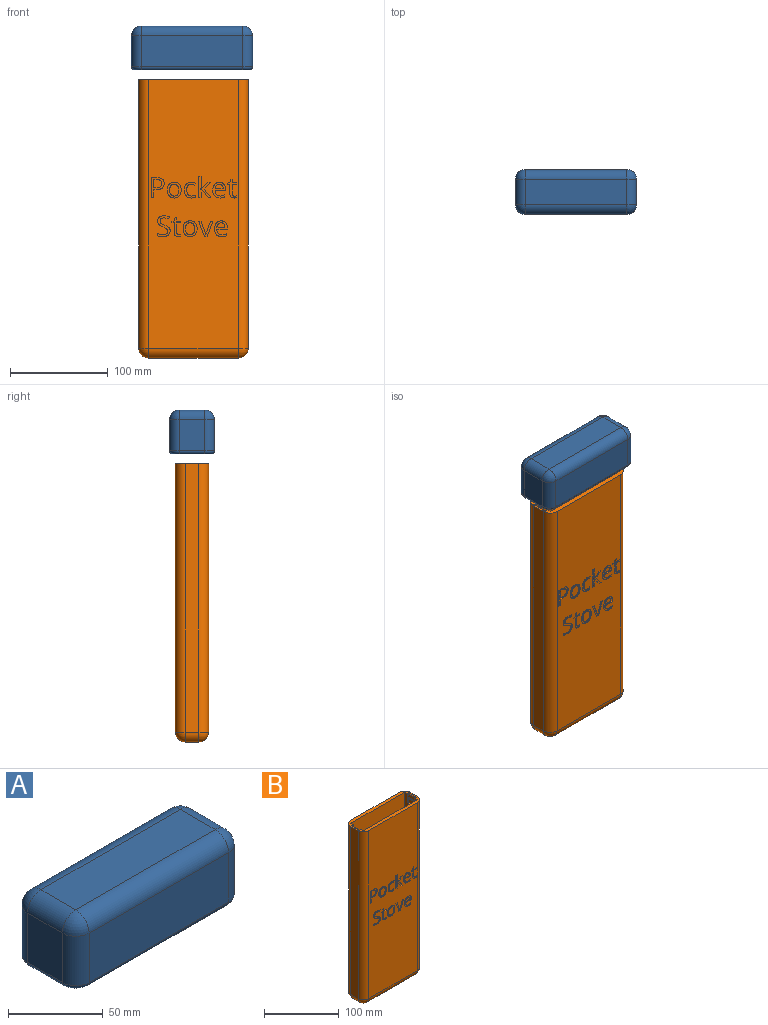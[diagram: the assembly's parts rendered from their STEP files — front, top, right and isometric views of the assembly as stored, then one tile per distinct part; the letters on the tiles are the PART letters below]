
ASSEMBLY  parts=2 mates=1
PART A: 47 faces, bbox 125.6x47.6x44.9 mm
  f0: plane 40x16mm, normal (-1,0,0), area 437.9mm2, adj f18,f19,f23,f24,f39,f41,f42,f43
  f1: plane 104x31.9mm, normal (0,1,0), area 3317.6mm2, adj f5,f8,f15,f32
  f2: plane 31.9x26mm, normal (-1,0,0), area 829.4mm2, adj f5,f6,f11,f28
  f3: plane 104x31.9mm, normal (0,-1,0), area 3317.6mm2, adj f6,f7,f12,f29
  f4: plane 31.9x26mm, normal (1,0,0), area 829.4mm2, adj f7,f8,f16,f33
  f5: cylinder r=10mm len=31.9mm, axis (0,0,-1), area 501.1mm2, adj f1,f2,f13,f30
  f6: cylinder r=10mm len=31.9mm, axis (0,0,1), area 501.1mm2, adj f2,f3,f10,f27
  f7: cylinder r=10mm len=31.9mm, axis (0,0,-1), area 501.1mm2, adj f3,f4,f14,f31
  f8: cylinder r=10mm len=31.9mm, axis (0,0,1), area 501.1mm2, adj f1,f4,f17,f34
  f9: plane 104x26mm, normal (0,0,1), area 2704mm2, adj f11,f12,f15,f16
  f10: sphere r=10mm, area 157.1mm2, adj f6,f11,f12
  f11: cylinder r=10mm len=26mm, axis (0,1,0), area 408.4mm2, adj f2,f9,f10,f13
  f12: cylinder r=10mm len=104mm, axis (-1,0,0), area 1633.6mm2, adj f3,f9,f10,f14
  f13: sphere r=10mm, area 157.1mm2, adj f5,f11,f15
  f14: sphere r=10mm, area 157.1mm2, adj f7,f12,f16
  f15: cylinder r=10mm len=104mm, axis (1,0,0), area 1633.6mm2, adj f1,f9,f13,f17
  f16: cylinder r=10mm len=26mm, axis (0,-1,0), area 408.4mm2, adj f4,f9,f14,f17
  f17: sphere r=10mm, area 157.1mm2, adj f8,f15,f16
  f18: plane 118x40mm, normal (0,0,-1), area 659.8mm2, adj f0,f20,f21,f22,f23,f24,f25,f26
  f19: plane 114x36mm, normal (0,0,-1), area 3883.2mm2, adj f0,f20,f21,f22,f23,f24,f25,f26
  f20: plane 40x16mm, normal (1,0,0), area 437.9mm2, adj f18,f19,f21,f26,f36,f37,f38,f45
  f21: cylinder r=10mm len=40mm, axis (0,0,-1), area 628.3mm2, adj f18,f19,f20,f22
  f22: plane 94x40mm, normal (0,-1,0), area 3760mm2, adj f18,f19,f21,f23
  f23: cylinder r=10mm len=40mm, axis (0,0,-1), area 628.3mm2, adj f0,f18,f19,f22
  f24: cylinder r=10mm len=40mm, axis (0,0,-1), area 628.3mm2, adj f0,f18,f19,f25
  f25: plane 94x40mm, normal (0,1,0), area 3760mm2, adj f18,f19,f24,f26
  f26: cylinder r=10mm len=40mm, axis (0,0,-1), area 628.3mm2, adj f18,f19,f20,f25
  f27: torus R=7mm, axis (0,0,1), area 66mm2, adj f6,f18,f28,f29
  f28: cylinder r=3mm len=26mm, axis (0,-1,0), area 122.5mm2, adj f2,f18,f27,f30
  f29: cylinder r=3mm len=104mm, axis (1,0,0), area 490.1mm2, adj f3,f18,f27,f31
  f30: torus R=7mm, axis (0,0,1), area 66mm2, adj f5,f18,f28,f32
  f31: torus R=7mm, axis (0,0,1), area 66mm2, adj f7,f18,f29,f33
  f32: cylinder r=3mm len=104mm, axis (-1,0,0), area 490.1mm2, adj f1,f18,f30,f34
  f33: cylinder r=3mm len=26mm, axis (0,1,0), area 122.5mm2, adj f4,f18,f31,f34
  f34: torus R=7mm, axis (0,0,1), area 66mm2, adj f8,f18,f32,f33
  f35: plane 15x13.5mm, normal (1,0,0), area 202.1mm2, adj f19,f36,f37,f38,f45,f46
  f36: plane 14x5mm, normal (0,-1,0), area 70mm2, adj f19,f20,f35,f45
  f37: plane 14x5mm, normal (0,1,0), area 70mm2, adj f19,f20,f35,f46
  f38: plane 11.5x5mm, normal (0,0,-1), area 57.5mm2, adj f20,f35,f45,f46
  f39: plane 14x5mm, normal (0,-1,0), area 70mm2, adj f0,f19,f40,f44
  f40: plane 15x13.5mm, normal (-1,0,0), area 202.1mm2, adj f19,f39,f41,f42,f43,f44
  f41: plane 14x5mm, normal (0,1,0), area 70mm2, adj f0,f19,f40,f43
  f42: plane 11.5x5mm, normal (0,0,-1), area 57.5mm2, adj f0,f40,f43,f44
  f43: cylinder r=1mm len=5mm, axis (-1,0,0), area 7.9mm2, adj f0,f40,f41,f42
  f44: cylinder r=1mm len=5mm, axis (1,0,0), area 7.9mm2, adj f0,f39,f40,f42
  f45: cylinder r=1mm len=5mm, axis (1,0,0), area 7.9mm2, adj f20,f35,f36,f38
  f46: cylinder r=1mm len=5mm, axis (-1,0,0), area 7.9mm2, adj f20,f35,f37,f38
PART B: 255 faces, bbox 112x34x285 mm
  f0: plane 14x6.27mm, normal (-1,0,0), area 77.1mm2, adj f5,f6,f32,f241,f242,f253
  f1: plane 14x5.12mm, normal (-1,0,0), area 71.6mm2, adj f5,f6,f245,f252
  f2: plane 14x6.27mm, normal (1,0,0), area 77.1mm2, adj f4,f30,f31,f239,f240,f254
  f3: plane 14x5.12mm, normal (1,0,0), area 71.6mm2, adj f30,f31,f246,f249
  f4: plane 4x2mm, normal (0,0,1), area 8mm2, adj f2,f10,f239,f240
  f5: plane 8.8x2.55mm, normal (0,-1,0), area 18.2mm2, adj f0,f1,f12,f241,f244,f245,f250,f253
  f6: plane 8.8x2.55mm, normal (0,1,0), area 18.2mm2, adj f0,f1,f12,f242,f244,f245,f251,f253
  f7: plane 275x92mm, normal (0,-1,0), area 24044.4mm2, adj f16,f18,f20,f21,f33,f34,f35,f36
  f8: plane 275x14mm, normal (-1,0,0), area 3850mm2, adj f16,f20,f26,f29
  f9: plane 275x14mm, normal (1,0,0), area 3850mm2, adj f16,f18,f22,f23
  f10: plane 280x24mm, normal (1,0,0), area 6520.1mm2, adj f4,f13,f14,f16,f17,f30,f31,f239
  f11: plane 92x14mm, normal (0,0,-1), area 1288mm2, adj f21,f22,f26,f27
  f12: plane 280x24mm, normal (-1,0,0), area 6520.1mm2, adj f5,f6,f13,f14,f16,f17,f32,f241
  f13: plane 280x102mm, normal (0,-1,0), area 28560mm2, adj f10,f12,f16,f17
  f14: plane 280x102mm, normal (0,1,0), area 28560mm2, adj f10,f12,f16,f17
  f15: plane 275x92mm, normal (0,1,0), area 25300mm2, adj f16,f23,f27,f29
  f16: plane 112x34mm, normal (0,0,1), area 1169.2mm2, adj f7,f8,f9,f10,f12,f13,f14,f15
  f17: plane 102x24mm, normal (0,0,1), area 2448mm2, adj f10,f12,f13,f14
  f18: cylinder r=10mm len=275mm, axis (0,0,-1), area 4319.7mm2, adj f7,f9,f16,f19
  f19: sphere r=10mm, area 157.1mm2, adj f18,f21,f22
  f20: cylinder r=10mm len=275mm, axis (0,0,1), area 4319.7mm2, adj f7,f8,f16,f24
  f21: cylinder r=10mm len=92mm, axis (1,0,0), area 1445.1mm2, adj f7,f11,f19,f24
  f22: cylinder r=10mm len=14mm, axis (0,1,0), area 219.9mm2, adj f9,f11,f19,f25
  f23: cylinder r=10mm len=275mm, axis (0,0,1), area 4319.7mm2, adj f9,f15,f16,f25
  f24: sphere r=10mm, area 157.1mm2, adj f20,f21,f26
  f25: sphere r=10mm, area 157.1mm2, adj f22,f23,f27
  f26: cylinder r=10mm len=14mm, axis (0,-1,0), area 219.9mm2, adj f8,f11,f24,f28
  f27: cylinder r=10mm len=92mm, axis (-1,0,0), area 1445.1mm2, adj f11,f15,f25,f28
  f28: sphere r=10mm, area 157.1mm2, adj f26,f27,f29
  f29: cylinder r=10mm len=275mm, axis (0,0,-1), area 4319.7mm2, adj f8,f15,f16,f28
  f30: plane 8.8x2.55mm, normal (0,-1,0), area 18.2mm2, adj f2,f3,f10,f239,f243,f246,f247,f254
  f31: plane 8.8x2.55mm, normal (0,1,0), area 18.2mm2, adj f2,f3,f10,f240,f243,f246,f248,f254
  f32: plane 4x2mm, normal (0,0,1), area 8mm2, adj f0,f12,f241,f242
  f33: extruded ~5.23x2.08mm, area 5.8mm2, adj f7,f34,f47,f48
  f34: extruded ~3.93x1mm, area 4.1mm2, adj f7,f33,f35,f48
  f35: plane 2.08x1mm, normal (-1,0,0), area 2.1mm2, adj f7,f34,f36,f48
  f36: extruded ~3.99x1mm, area 4.1mm2, adj f7,f35,f37,f48
  f37: extruded ~3.43x1.53mm, area 3.9mm2, adj f7,f36,f38,f48
  f38: extruded ~4.4x1.16mm, area 4.6mm2, adj f7,f37,f39,f48
  f39: extruded ~6.05x4.74mm, area 8.8mm2, adj f7,f38,f40,f48
  f40: extruded ~1.63x1mm, area 1.6mm2, adj f7,f39,f41,f48
  f41: extruded ~1.7x1mm, area 1.8mm2, adj f7,f40,f42,f48
  f42: plane 2x1mm, normal (-0.94,0,0.34), area 2.1mm2, adj f7,f41,f43,f48
  f43: extruded ~1.76x1mm, area 1.9mm2, adj f7,f42,f44,f48
  f44: extruded ~2.24x1mm, area 2.3mm2, adj f7,f43,f45,f48
  f45: extruded ~5.36x2.13mm, area 6mm2, adj f7,f44,f46,f48
  f46: extruded ~6.03x1.88mm, area 6.5mm2, adj f7,f45,f47,f48
  f47: extruded ~5.89x1.85mm, area 6.3mm2, adj f7,f33,f46,f48
  f48: plane 16.13x11.24mm, normal (0,-1,0), area 64.2mm2, adj f33,f34,f35,f36,f37,f38,f39,f40
  f49: extruded ~2.99x1.22mm, area 3.3mm2, adj f50,f67,f68,f234
  f50: extruded ~2.84x1.19mm, area 3.2mm2, adj f49,f51,f68,f234
  f51: extruded ~3.41x1mm, area 3.6mm2, adj f50,f52,f68,f234
  f52: plane 8.13x1mm, normal (0,0,-1), area 8.1mm2, adj f51,f67,f68,f234
  f53: extruded ~5.44x2.1mm, area 6mm2, adj f7,f54,f66,f68
  f54: extruded ~2.69x1mm, area 2.7mm2, adj f7,f53,f55,f68
  f55: extruded ~2.36x1mm, area 2.5mm2, adj f7,f54,f56,f68
  f56: plane 2.1x1mm, normal (-1,0,0), area 2.1mm2, adj f7,f55,f57,f68
  f57: extruded ~4.96x1.05mm, area 5.1mm2, adj f7,f56,f58,f68
  f58: extruded ~3.7x1.42mm, area 4.1mm2, adj f7,f57,f59,f68
  f59: extruded ~4.16x1.39mm, area 4.5mm2, adj f7,f58,f60,f68
  f60: plane 10.71x1mm, normal (0,0,1), area 10.7mm2, adj f7,f59,f61,f68
  f61: plane 1.49x1mm, normal (-1,0,0), area 1.5mm2, adj f7,f60,f62,f68
  f62: extruded ~5.08x1.7mm, area 5.5mm2, adj f7,f61,f63,f68
  f63: extruded ~4.62x1.92mm, area 5.2mm2, adj f7,f62,f64,f68
  f64: extruded ~4.98x2.21mm, area 5.6mm2, adj f7,f63,f65,f68
  f65: extruded ~5.98x1.85mm, area 6.4mm2, adj f7,f64,f66,f68
  f66: extruded ~5.83x2mm, area 6.3mm2, adj f7,f53,f65,f68
  f67: extruded ~3.38x1.32mm, area 3.7mm2, adj f49,f52,f68,f234
  f68: plane 16.13x13.16mm, normal (0,-1,0), area 96.5mm2, adj f49,f50,f51,f52,f53,f54,f55,f56
  f69: extruded ~4.54x1.19mm, area 4.8mm2, adj f70,f85,f86,f235
  f70: extruded ~4.53x1.18mm, area 4.8mm2, adj f69,f71,f86,f235
  f71: extruded ~3.49x1.52mm, area 4mm2, adj f70,f72,f86,f235
  f72: extruded ~3.54x1.54mm, area 4mm2, adj f71,f73,f86,f235
  f73: extruded ~4.51x1.2mm, area 4.7mm2, adj f72,f74,f86,f235
  f74: extruded ~4.55x1.2mm, area 4.8mm2, adj f73,f75,f86,f235
  f75: extruded ~3.52x1.55mm, area 4mm2, adj f74,f85,f86,f235
  f76: extruded ~5.94x1.91mm, area 6.4mm2, adj f7,f77,f84,f86
  f77: extruded ~5.88x1.92mm, area 6.3mm2, adj f7,f76,f78,f86
  f78: extruded ~5.18x2.17mm, area 5.8mm2, adj f7,f77,f79,f86
  f79: extruded ~5.28x2.12mm, area 5.9mm2, adj f7,f78,f80,f86
  f80: extruded ~5.93x1.9mm, area 6.4mm2, adj f7,f79,f81,f86
  f81: extruded ~4.29x1mm, area 4.4mm2, adj f7,f80,f82,f86
  f82: extruded ~2.81x2.5mm, area 3.8mm2, adj f7,f81,f83,f86
  f83: extruded ~3.71x1mm, area 3.9mm2, adj f7,f82,f84,f86
  f84: extruded ~5.29x2.14mm, area 5.9mm2, adj f7,f76,f83,f86
  f85: extruded ~3.5x1.56mm, area 4mm2, adj f69,f75,f86,f235
  f86: plane 16.13x14.29mm, normal (0,-1,0), area 93mm2, adj f69,f70,f71,f72,f73,f74,f75,f76
  f87: extruded ~2.27x1.86mm, area 2.9mm2, adj f7,f88,f101,f102
  f88: plane 1x0.11mm, normal (0,0,-1), area 0.1mm2, adj f7,f87,f89,f102
  f89: extruded ~2.41x1mm, area 2.4mm2, adj f7,f88,f90,f102
  f90: plane 11.71x1mm, normal (-1,0,0), area 11.7mm2, adj f7,f89,f91,f102
  f91: plane 2.33x1mm, normal (0,0,-1), area 2.3mm2, adj f7,f90,f92,f102
  f92: plane 22.09x1mm, normal (1,0,0), area 22.1mm2, adj f7,f91,f93,f102
  f93: plane 2.33x1mm, normal (0,0,1), area 2.3mm2, adj f7,f92,f94,f102
  f94: plane 5.82x1mm, normal (-1,0,0), area 5.8mm2, adj f7,f93,f95,f102
  f95: plane 1.77x1.54mm, normal (-0.65,0,0.76), area 2.3mm2, adj f7,f94,f96,f102
  f96: plane 7.35x5.5mm, normal (0.8,0,0.6), area 9.2mm2, adj f7,f95,f97,f102
  f97: plane 2.85x1mm, normal (0,0,1), area 2.9mm2, adj f7,f96,f98,f102
  f98: plane 8.93x6.74mm, normal (-0.8,0,-0.6), area 11.2mm2, adj f7,f97,f99,f102
  f99: plane 6.63x6.3mm, normal (-0.72,0,0.69), area 9.1mm2, adj f7,f98,f100,f102
  f100: plane 2.8x1mm, normal (0,0,-1), area 2.8mm2, adj f7,f99,f101,f102
  f101: plane 5.32x5.02mm, normal (0.73,0,-0.69), area 7.3mm2, adj f7,f87,f100,f102
  f102: plane 22.09x12.45mm, normal (0,-1,0), area 97.7mm2, adj f87,f88,f89,f90,f91,f92,f93,f94
  f103: extruded ~1.21x1mm, area 1.2mm2, adj f7,f104,f121,f122
  f104: extruded ~1.83x1mm, area 2mm2, adj f7,f103,f105,f122
  f105: extruded ~2.16x1mm, area 2.3mm2, adj f7,f104,f106,f122
  f106: plane 9.16x1mm, normal (-1,0,0), area 9.2mm2, adj f7,f105,f107,f122
  f107: plane 4.51x1mm, normal (0,0,1), area 4.5mm2, adj f7,f106,f108,f122
  f108: plane 1.83x1mm, normal (-1,0,0), area 1.8mm2, adj f7,f107,f109,f122
  f109: plane 4.51x1mm, normal (0,0,-1), area 4.5mm2, adj f7,f108,f110,f122
  f110: plane 3.61x1mm, normal (-1,0,0), area 3.6mm2, adj f7,f109,f111,f122
  f111: plane 1.36x1mm, normal (0,0,-1), area 1.4mm2, adj f7,f110,f112,f122
  f112: plane 3.32x1mm, normal (0.96,0,-0.29), area 3.5mm2, adj f7,f111,f113,f122
  f113: plane 2.23x1mm, normal (0.4,0,-0.92), area 2.4mm2, adj f7,f112,f114,f122
  f114: plane 1.14x1mm, normal (1,0,0), area 1.1mm2, adj f7,f113,f115,f122
  f115: plane 2.23x1mm, normal (0,0,1), area 2.2mm2, adj f7,f114,f116,f122
  f116: plane 9.26x1mm, normal (1,0,0), area 9.3mm2, adj f7,f115,f117,f122
  f117: extruded ~4.76x4.51mm, area 7.5mm2, adj f7,f116,f118,f122
  f118: extruded ~1.34x1mm, area 1.4mm2, adj f7,f117,f119,f122
  f119: extruded ~1.13x1mm, area 1.2mm2, adj f7,f118,f120,f122
  f120: plane 1.8x1mm, normal (-1,0,0), area 1.8mm2, adj f7,f119,f121,f122
  f121: extruded ~1x0.92mm, area 0.9mm2, adj f7,f103,f120,f122
  f122: plane 19.45x9.21mm, normal (0,-1,0), area 62.6mm2, adj f103,f104,f105,f106,f107,f108,f109,f110
  f123: extruded ~4.27x1.99mm, area 4.9mm2, adj f7,f124,f147,f148
  f124: extruded ~3.46x1.23mm, area 3.8mm2, adj f7,f123,f125,f148
  f125: extruded ~4.49x2.5mm, area 5.2mm2, adj f7,f124,f126,f148
  f126: extruded ~2.89x1.27mm, area 3.2mm2, adj f7,f125,f127,f148
  f127: extruded ~1.34x1.27mm, area 1.9mm2, adj f7,f126,f128,f148
  f128: extruded ~1.77x1mm, area 1.8mm2, adj f7,f127,f129,f148
  f129: extruded ~2.28x1.08mm, area 2.6mm2, adj f7,f128,f130,f148
  f130: extruded ~3x1mm, area 3.2mm2, adj f7,f129,f131,f148
  f131: extruded ~5x1.08mm, area 5.1mm2, adj f7,f130,f132,f148
  f132: plane 2.1x1mm, normal (-0.94,0,0.34), area 2.2mm2, adj f7,f131,f133,f148
  f133: extruded ~5.69x1.14mm, area 5.8mm2, adj f7,f132,f134,f148
  f134: extruded ~4.77x1.42mm, area 5.1mm2, adj f7,f133,f135,f148
  f135: extruded ~3.82x1.8mm, area 4.4mm2, adj f7,f134,f136,f148
  f136: extruded ~3.7x1.24mm, area 4mm2, adj f7,f135,f137,f148
  f137: extruded ~4.14x2.46mm, area 4.9mm2, adj f7,f136,f138,f148
  f138: extruded ~3.09x1.32mm, area 3.4mm2, adj f7,f137,f139,f148
  f139: extruded ~1.45x1.27mm, area 1.9mm2, adj f7,f138,f140,f148
  f140: extruded ~1.76x1mm, area 1.8mm2, adj f7,f139,f141,f148
  f141: extruded ~2.55x1.22mm, area 2.9mm2, adj f7,f140,f142,f148
  f142: extruded ~3.63x1mm, area 3.8mm2, adj f7,f141,f143,f148
  f143: extruded ~2.98x1mm, area 3mm2, adj f7,f142,f144,f148
  f144: extruded ~2.78x1mm, area 2.9mm2, adj f7,f143,f145,f148
  f145: plane 2.33x1mm, normal (1,0,0), area 2.3mm2, adj f7,f144,f146,f148
  f146: extruded ~5.68x1mm, area 5.8mm2, adj f7,f145,f147,f148
  f147: extruded ~5.39x1.54mm, area 5.7mm2, adj f7,f123,f146,f148
  f148: plane 21.33x13.06mm, normal (0,-1,0), area 99.7mm2, adj f123,f124,f125,f126,f127,f128,f129,f130
  f149: extruded ~1.21x1mm, area 1.2mm2, adj f7,f150,f167,f168
  f150: extruded ~1.83x1mm, area 2mm2, adj f7,f149,f151,f168
  f151: extruded ~2.16x1mm, area 2.3mm2, adj f7,f150,f152,f168
  f152: plane 9.16x1mm, normal (-1,0,0), area 9.2mm2, adj f7,f151,f153,f168
  f153: plane 4.51x1mm, normal (0,0,1), area 4.5mm2, adj f7,f152,f154,f168
  f154: plane 1.83x1mm, normal (-1,0,0), area 1.8mm2, adj f7,f153,f155,f168
  f155: plane 4.51x1mm, normal (0,0,-1), area 4.5mm2, adj f7,f154,f156,f168
  f156: plane 3.61x1mm, normal (-1,0,0), area 3.6mm2, adj f7,f155,f157,f168
  f157: plane 1.36x1mm, normal (0,0,-1), area 1.4mm2, adj f7,f156,f158,f168
  f158: plane 3.32x1mm, normal (0.96,0,-0.29), area 3.5mm2, adj f7,f157,f159,f168
  f159: plane 2.23x1mm, normal (0.4,0,-0.92), area 2.4mm2, adj f7,f158,f160,f168
  f160: plane 1.14x1mm, normal (1,0,0), area 1.1mm2, adj f7,f159,f161,f168
  f161: plane 2.23x1mm, normal (0,0,1), area 2.2mm2, adj f7,f160,f162,f168
  f162: plane 9.26x1mm, normal (1,0,0), area 9.3mm2, adj f7,f161,f163,f168
  f163: extruded ~4.76x4.51mm, area 7.5mm2, adj f7,f162,f164,f168
  f164: extruded ~1.34x1mm, area 1.4mm2, adj f7,f163,f165,f168
  f165: extruded ~1.13x1mm, area 1.2mm2, adj f7,f164,f166,f168
  f166: plane 1.8x1mm, normal (-1,0,0), area 1.8mm2, adj f7,f165,f167,f168
  f167: extruded ~1x0.92mm, area 0.9mm2, adj f7,f149,f166,f168
  f168: plane 19.45x9.21mm, normal (0,-1,0), area 62.6mm2, adj f149,f150,f151,f152,f153,f154,f155,f156
  f169: extruded ~2.99x1.22mm, area 3.3mm2, adj f170,f187,f188,f236
  f170: extruded ~2.84x1.19mm, area 3.2mm2, adj f169,f171,f188,f236
  f171: extruded ~3.41x1mm, area 3.6mm2, adj f170,f172,f188,f236
  f172: plane 8.13x1mm, normal (0,0,-1), area 8.1mm2, adj f171,f187,f188,f236
  f173: extruded ~5.44x2.1mm, area 6mm2, adj f7,f174,f186,f188
  f174: extruded ~2.69x1mm, area 2.7mm2, adj f7,f173,f175,f188
  f175: extruded ~2.36x1mm, area 2.5mm2, adj f7,f174,f176,f188
  f176: plane 2.1x1mm, normal (-1,0,0), area 2.1mm2, adj f7,f175,f177,f188
  f177: extruded ~4.96x1.05mm, area 5.1mm2, adj f7,f176,f178,f188
  f178: extruded ~3.7x1.42mm, area 4.1mm2, adj f7,f177,f179,f188
  f179: extruded ~4.16x1.39mm, area 4.5mm2, adj f7,f178,f180,f188
  f180: plane 10.71x1mm, normal (0,0,1), area 10.7mm2, adj f7,f179,f181,f188
  f181: plane 1.49x1mm, normal (-1,0,0), area 1.5mm2, adj f7,f180,f182,f188
  f182: extruded ~5.08x1.7mm, area 5.5mm2, adj f7,f181,f183,f188
  f183: extruded ~4.62x1.92mm, area 5.2mm2, adj f7,f182,f184,f188
  f184: extruded ~4.98x2.21mm, area 5.6mm2, adj f7,f183,f185,f188
  f185: extruded ~5.98x1.85mm, area 6.4mm2, adj f7,f184,f186,f188
  f186: extruded ~5.83x2mm, area 6.3mm2, adj f7,f173,f185,f188
  f187: extruded ~3.38x1.32mm, area 3.7mm2, adj f169,f172,f188,f236
  f188: plane 16.13x13.16mm, normal (0,-1,0), area 96.5mm2, adj f169,f170,f171,f172,f173,f174,f175,f176
  f189: extruded ~4.54x1.19mm, area 4.8mm2, adj f190,f205,f206,f237
  f190: extruded ~4.53x1.18mm, area 4.8mm2, adj f189,f191,f206,f237
  f191: extruded ~3.49x1.52mm, area 4mm2, adj f190,f192,f206,f237
  f192: extruded ~3.54x1.54mm, area 4mm2, adj f191,f193,f206,f237
  f193: extruded ~4.51x1.2mm, area 4.7mm2, adj f192,f194,f206,f237
  f194: extruded ~4.55x1.2mm, area 4.8mm2, adj f193,f195,f206,f237
  f195: extruded ~3.52x1.55mm, area 4mm2, adj f194,f205,f206,f237
  f196: extruded ~5.94x1.91mm, area 6.4mm2, adj f7,f197,f204,f206
  f197: extruded ~5.88x1.92mm, area 6.3mm2, adj f7,f196,f198,f206
  f198: extruded ~5.18x2.17mm, area 5.8mm2, adj f7,f197,f199,f206
  f199: extruded ~5.28x2.12mm, area 5.9mm2, adj f7,f198,f200,f206
  f200: extruded ~5.93x1.9mm, area 6.4mm2, adj f7,f199,f201,f206
  f201: extruded ~4.29x1mm, area 4.4mm2, adj f7,f200,f202,f206
  f202: extruded ~2.81x2.5mm, area 3.8mm2, adj f7,f201,f203,f206
  f203: extruded ~3.71x1mm, area 3.9mm2, adj f7,f202,f204,f206
  f204: extruded ~5.29x2.14mm, area 5.9mm2, adj f7,f196,f203,f206
  f205: extruded ~3.5x1.56mm, area 4mm2, adj f189,f195,f206,f237
  f206: plane 16.13x14.29mm, normal (0,-1,0), area 93mm2, adj f189,f190,f191,f192,f193,f194,f195,f196
  f207: plane 2.18x1mm, normal (0,0,-1), area 2.2mm2, adj f208,f221,f222,f238
  f208: plane 8.43x1mm, normal (-1,0,0), area 8.4mm2, adj f207,f209,f222,f238
  f209: plane 2.7x1mm, normal (0,0,1), area 2.7mm2, adj f208,f210,f222,f238
  f210: extruded ~4.2x1.01mm, area 4.4mm2, adj f209,f211,f222,f238
  f211: extruded ~3.06x1.35mm, area 3.5mm2, adj f210,f212,f222,f238
  f212: extruded ~3.32x1.43mm, area 3.8mm2, adj f211,f221,f222,f238
  f213: extruded ~4.85x2.15mm, area 5.5mm2, adj f7,f214,f220,f222
  f214: extruded ~7.78x6.05mm, area 11.3mm2, adj f7,f213,f215,f222
  f215: plane 5.38x1mm, normal (0,0,-1), area 5.4mm2, adj f7,f214,f216,f222
  f216: plane 20.75x1mm, normal (1,0,0), area 20.8mm2, adj f7,f215,f217,f222
  f217: plane 2.41x1mm, normal (0,0,1), area 2.4mm2, adj f7,f216,f218,f222
  f218: plane 8.16x1mm, normal (-1,0,0), area 8.2mm2, adj f7,f217,f219,f222
  f219: plane 2.44x1mm, normal (0,0,1), area 2.4mm2, adj f7,f218,f220,f222
  f220: extruded ~6.15x1.7mm, area 6.5mm2, adj f7,f213,f219,f222
  f221: extruded ~4.64x1.04mm, area 4.8mm2, adj f207,f212,f222,f238
  f222: plane 20.75x13.16mm, normal (0,-1,0), area 106.1mm2, adj f207,f208,f209,f210,f211,f212,f213,f214
  f223: plane 15.56x5.9mm, normal (0.93,0,0.35), area 16.6mm2, adj f7,f224,f232,f233
  f224: plane 2.75x1mm, normal (0,0,1), area 2.8mm2, adj f7,f223,f225,f233
  f225: plane 15.56x5.9mm, normal (-0.93,0,0.35), area 16.6mm2, adj f7,f224,f226,f233
  f226: plane 2.53x1mm, normal (0,0,-1), area 2.5mm2, adj f7,f225,f227,f233
  f227: extruded ~10.31x3.72mm, area 11mm2, adj f7,f226,f228,f233
  f228: extruded ~3.11x1mm, area 3.3mm2, adj f7,f227,f229,f233
  f229: plane 1x0.11mm, normal (0,0,-1), area 0.1mm2, adj f7,f228,f230,f233
  f230: extruded ~4.2x1.34mm, area 4.4mm2, adj f7,f229,f231,f233
  f231: plane 9.22x3.35mm, normal (-0.94,0,-0.34), area 9.8mm2, adj f7,f230,f232,f233
  f232: plane 2.53x1mm, normal (0,0,-1), area 2.5mm2, adj f7,f223,f231,f233
  f233: plane 15.56x14.56mm, normal (0,-1,0), area 72mm2, adj f223,f224,f225,f226,f227,f228,f229,f230
  f234: plane 8.13x4.6mm, normal (0,-1,0), area 30.1mm2, adj f49,f50,f51,f52,f67
  f235: plane 12.15x9.41mm, normal (0,-1,0), area 94.9mm2, adj f69,f70,f71,f72,f73,f74,f75,f85
  f236: plane 8.13x4.6mm, normal (0,-1,0), area 30.1mm2, adj f169,f170,f171,f172,f187
  f237: plane 12.15x9.41mm, normal (0,-1,0), area 94.9mm2, adj f189,f190,f191,f192,f193,f194,f195,f205
  f238: plane 8.43x8.25mm, normal (0,-1,0), area 61.8mm2, adj f207,f208,f209,f210,f211,f212,f221
  f239: cylinder r=5mm len=5mm, axis (-1,0,0), area 15.7mm2, adj f2,f4,f10,f30
  f240: cylinder r=5mm len=5mm, axis (1,0,0), area 15.7mm2, adj f2,f4,f10,f31
  f241: cylinder r=5mm len=5mm, axis (-1,0,0), area 15.7mm2, adj f0,f5,f12,f32
  f242: cylinder r=5mm len=5mm, axis (1,0,0), area 15.7mm2, adj f0,f6,f12,f32
  f243: cylinder r=0.55mm len=14mm, axis (0,1,0), area 13.2mm2, adj f30,f31,f246,f254
  f244: cylinder r=0.55mm len=14mm, axis (0,1,0), area 13.2mm2, adj f5,f6,f245,f253
  f245: cylinder r=1mm len=14mm, axis (0,1,0), area 12.2mm2, adj f1,f5,f6,f244
  f246: cylinder r=1mm len=14mm, axis (0,1,0), area 12.2mm2, adj f3,f30,f31,f243
  f247: cylinder r=1.2mm len=3.2mm, axis (1,0,0), area 4.6mm2, adj f10,f16,f30,f249
  f248: cylinder r=1.2mm len=3.2mm, axis (-1,0,0), area 4.6mm2, adj f10,f16,f31,f249
  f249: cylinder r=1.2mm len=16.4mm, axis (0,-1,0), area 28mm2, adj f3,f16,f247,f248
  f250: cylinder r=1.2mm len=3.2mm, axis (1,0,0), area 4.6mm2, adj f5,f12,f16,f252
  f251: cylinder r=1.2mm len=3.2mm, axis (-1,0,0), area 4.6mm2, adj f6,f12,f16,f252
  f252: cylinder r=1.2mm len=16.4mm, axis (0,1,0), area 28mm2, adj f1,f16,f250,f251
  f253: cylinder r=1.1mm len=14mm, axis (0,1,0), area 13mm2, adj f0,f5,f6,f244
  f254: cylinder r=1.1mm len=14mm, axis (0,1,0), area 13mm2, adj f2,f30,f31,f243
PLACE A t=(-42.56,108.34,65.87)mm
PLACE B t=(-41.06,108.34,45.87)mm fixed
MATE slider A.f42 <-> B.f32  axis (0,0,-1) through (11.94,108.34,365.87)mm
